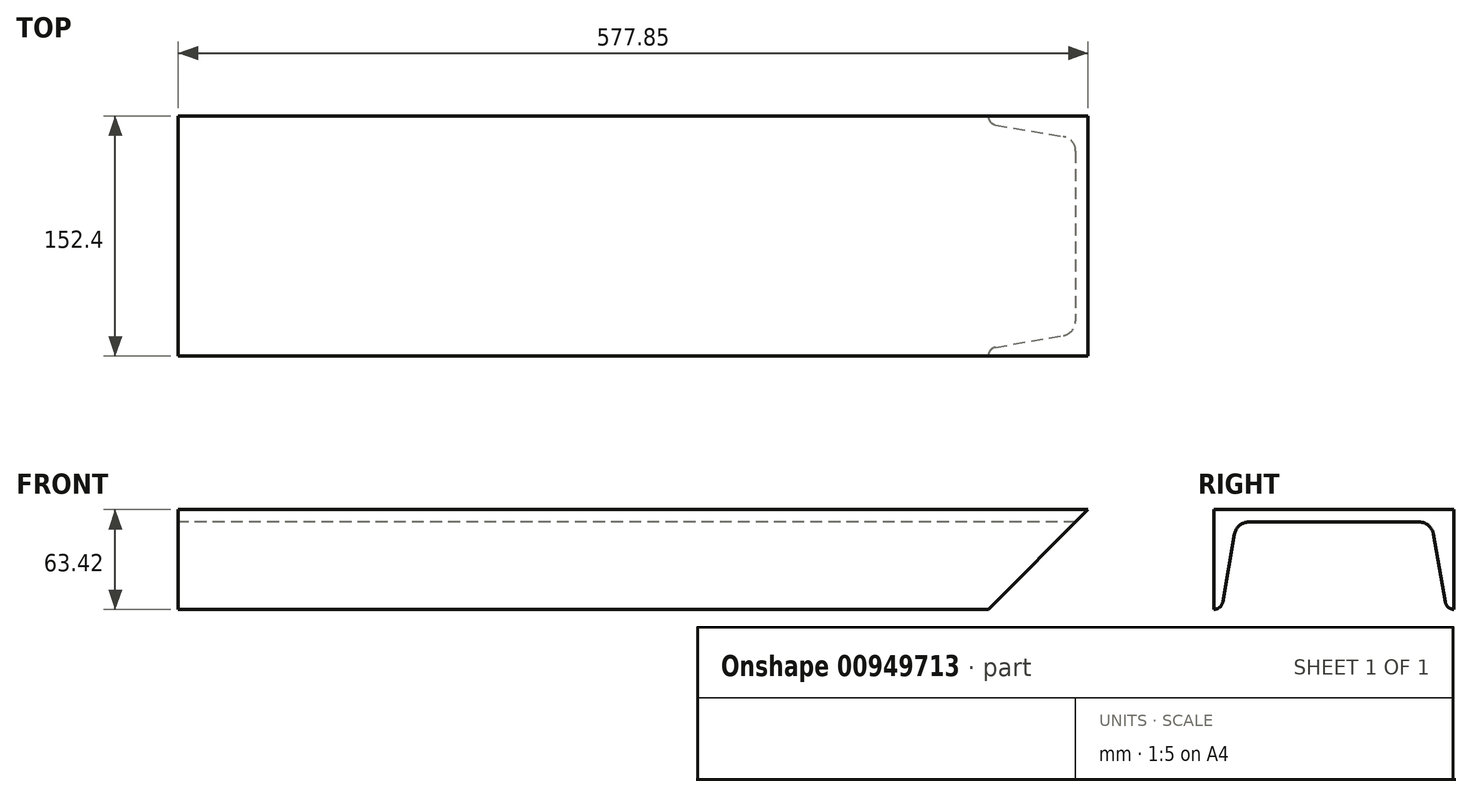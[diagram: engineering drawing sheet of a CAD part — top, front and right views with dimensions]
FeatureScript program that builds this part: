
annotation { "Feature Type Name" : "Feature", "Feature Type Description" : "" }
export const myFeature = defineFeature(function(context is Context, id is Id, definition is map)
    precondition{}
    {
        {
            var Q0;
            Q0=qCreatedBy(makeId("Right.planeOp"),FACE);
            var sketch = newSketch(context, id + "F0", { "sketchPlane" : qUnion([Q0])});
            skLineSegment(sketch, "E0", {"start": v(-76.2, 0) * mm, "end": v(76.2, 0) * mm});
            skLineSegment(sketch, "E1", {"start": v(76.2, 0) * mm, "end": v(76.2, -63.42) * mm});
            skLineSegment(sketch, "E2", {"start": v(-76.2, 0) * mm, "end": v(-76.2, -63.42) * mm});
            skLineSegment(sketch, "E3", {"start": v(-63.12, -15.57) * mm, "end": v(-70.65, -58.76) * mm});
            skLineSegment(sketch, "E4", {"start": v(63.12, -15.57) * mm, "end": v(70.65, -58.76) * mm});
            skLineSegment(sketch, "E5", {"start": v(-53.98, -7.87) * mm, "end": v(53.98, -7.87) * mm});
            skArc(sketch, "E6.filletArc", {"start": v(-76.2, -63.42) * mm, "mid": v(-72.57, -62.1) * mm, "end": v(-70.65, -58.76) * mm});
            skArc(sketch, "E7.filletArc", {"start": v(70.65, -58.76) * mm, "mid": v(72.57, -62.1) * mm, "end": v(76.2, -63.42) * mm});
            skArc(sketch, "E8.filletArc", {"start": v(-53.98, -7.87) * mm, "mid": v(-59.95, -10.05) * mm, "end": v(-63.12, -15.57) * mm});
            skArc(sketch, "E9.filletArc", {"start": v(63.12, -15.57) * mm, "mid": v(59.95, -10.05) * mm, "end": v(53.98, -7.87) * mm});
            skSolve(sketch);
        }
        {
            var Q0;
            Q0=qSketchRegion(id+"F0",true);
            extrude(context, id + "F1", {"entities" : qUnion([Q0]), "depth" : 577.85 * mm, "offsetDistance" : 25.4 * mm});
        }
        {
            var Q0;
            Q0=qCreatedBy(makeId("Front.planeOp"),FACE);
            var sketch = newSketch(context, id + "F2", { "sketchPlane" : qUnion([Q0])});
            skLineSegment(sketch, "E10", {"start": v(577.85, 0) * mm, "end": v(577.85, -63.42) * mm});
            skLineSegment(sketch, "E11", {"start": v(577.85, -63.42) * mm, "end": v(514.43, -63.42) * mm});
            skLineSegment(sketch, "E12", {"start": v(514.43, -63.42) * mm, "end": v(577.85, 0) * mm});
            skSolve(sketch);
        }
        {
            var Q0;
            Q0=qSketchRegion(id+"F2",true);
            extrude(context, id + "F3", {"entities" : qUnion([Q0]), "operationType" : NewBodyOperationType.REMOVE, "endBound" : BoundingType.THROUGH_ALL, "depth" : 25.4 * mm, "offsetDistance" : 25.4 * mm, "hasSecondDirection" : true, "secondDirectionBound" : SecondDirectionBoundingType.THROUGH_ALL, "secondDirectionOppositeDirection" : true, "secondDirectionDepth" : 25.4 * mm});
        }
    });
